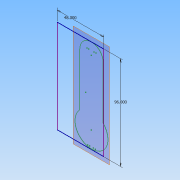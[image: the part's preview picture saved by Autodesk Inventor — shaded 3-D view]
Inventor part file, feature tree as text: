
AUTODESK INVENTOR PART (.ipt)
format: ipt  version: 2013 (Build 170138000, 138)  size: 83,968 bytes
history: native  units: in
note: dims shown in document units (in); Inventor stores cm internally (conversion verified against a paired STEP export)
features: plane x1, extrude x1, sketch x1, reference x1
ambient origin geometry x8: Origin, YZ Plane, XZ Plane, XY Plane, X Axis, Y Axis, Z Axis, Center Point
bodies: Solid1 (feature_tree)
feature tree (4):
  plane  "Work Plane1"
  extrude  "Extrusion1"  Depth=96.0in
  sketch  "Sketch1"  dims[d0=48.0in d2=96.0in d3=0.75in d4=0.0in]
  reference  "Reference1"
